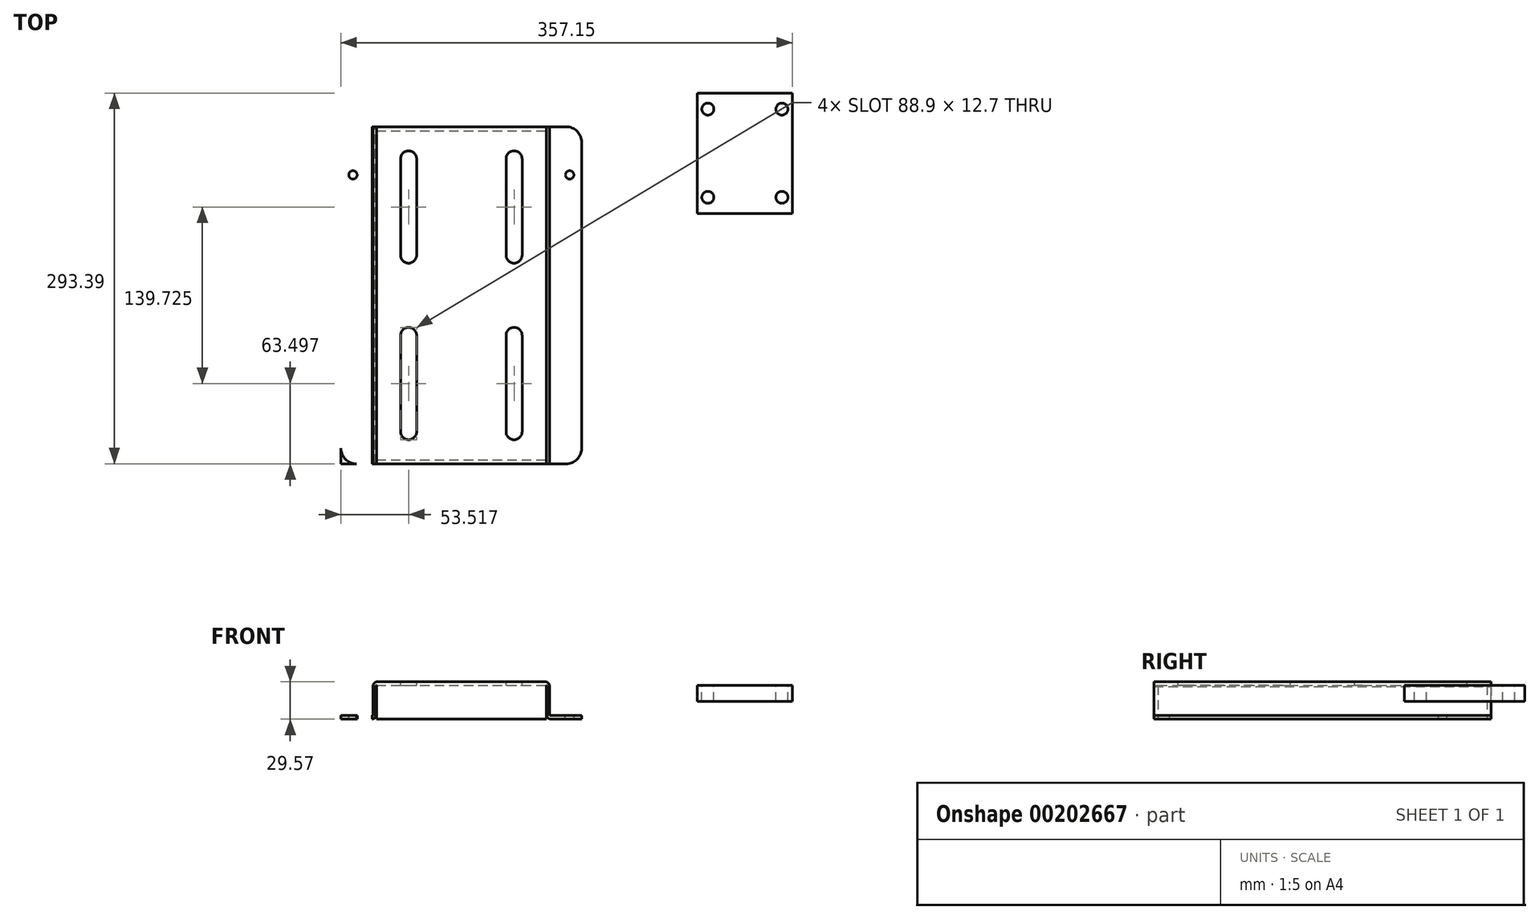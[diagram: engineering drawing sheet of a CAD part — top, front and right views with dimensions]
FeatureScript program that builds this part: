
annotation { "Feature Type Name" : "Feature", "Feature Type Description" : "" }
export const myFeature = defineFeature(function(context is Context, id is Id, definition is map)
    precondition{}
    {
        {
            var Q0;
            Q0=qCreatedBy(makeId("Front.planeOp"),FACE);
            var sketch = newSketch(context, id + "F0", { "sketchPlane" : qUnion([Q0])});
            skLineSegment(sketch, "E0", {"start": v(497.25, 316.92) * mm, "end": v(496.14, 315.8) * mm});
            skLineSegment(sketch, "E1", {"start": v(496.14, 298.54) * mm, "end": v(497.25, 297.42) * mm});
            skLineSegment(sketch, "E2", {"start": v(506.12, 296.17) * mm, "end": v(508.12, 296.17) * mm});
            skLineSegment(sketch, "E3", {"start": v(508.12, 318.17) * mm, "end": v(506.12, 318.17) * mm});
            skLineSegment(sketch, "E4", {"start": v(514.93, 297.83) * mm, "end": v(516.85, 299.75) * mm});
            skLineSegment(sketch, "E5", {"start": v(516.85, 314.6) * mm, "end": v(514.86, 316.59) * mm});
            skLineSegment(sketch, "E6", {"start": v(408.26, 311.93) * mm, "end": v(407.26, 310.93) * mm});
            skLineSegment(sketch, "E7", {"start": v(407.26, 303.4) * mm, "end": v(408.26, 302.41) * mm});
            skLineSegment(sketch, "E8", {"start": v(508.85, 311.93) * mm, "end": v(508.12, 311.93) * mm});
            skLineSegment(sketch, "E9", {"start": v(496.14, 311.93) * mm, "end": v(430.37, 311.93) * mm});
            skLineSegment(sketch, "E10", {"start": v(411.15, 311.93) * mm, "end": v(408.26, 311.93) * mm});
            skLineSegment(sketch, "E11", {"start": v(408.26, 302.41) * mm, "end": v(411.31, 302.41) * mm});
            skLineSegment(sketch, "E12", {"start": v(430.18, 302.41) * mm, "end": v(496.14, 302.41) * mm});
            skLineSegment(sketch, "E13", {"start": v(508.12, 302.41) * mm, "end": v(508.85, 302.41) * mm});
            skLineSegment(sketch, "E14", {"start": v(413.53, 317.08) * mm, "end": v(413.53, 297.08) * mm});
            skLineSegment(sketch, "E15", {"start": v(415.57, 317.08) * mm, "end": v(413.53, 317.08) * mm});
            skLineSegment(sketch, "E16", {"start": v(415.57, 317.08) * mm, "end": v(415.57, 297.08) * mm});
            skLineSegment(sketch, "E17", {"start": v(415.57, 297.08) * mm, "end": v(413.53, 297.08) * mm});
            skLineSegment(sketch, "E18", {"start": v(424.65, 317.08) * mm, "end": v(415.57, 317.08) * mm});
            skLineSegment(sketch, "E19", {"start": v(424.65, 317.08) * mm, "end": v(424.65, 297.08) * mm});
            skLineSegment(sketch, "E20", {"start": v(424.65, 297.08) * mm, "end": v(415.57, 297.08) * mm});
            skLineSegment(sketch, "E21", {"start": v(426.63, 317.08) * mm, "end": v(424.65, 317.08) * mm});
            skLineSegment(sketch, "E22", {"start": v(426.63, 317.08) * mm, "end": v(426.63, 297.08) * mm});
            skLineSegment(sketch, "E23", {"start": v(426.63, 297.08) * mm, "end": v(424.65, 297.08) * mm});
            skLineSegment(sketch, "E24", {"start": v(431.3, 312.33) * mm, "end": v(430.67, 312.15) * mm});
            skLineSegment(sketch, "E25", {"start": v(430.67, 312.15) * mm, "end": v(430.07, 311.63) * mm});
            skLineSegment(sketch, "E26", {"start": v(430.07, 311.63) * mm, "end": v(429.56, 310.8) * mm});
            skLineSegment(sketch, "E27", {"start": v(429.56, 310.8) * mm, "end": v(429.17, 309.7) * mm});
            skLineSegment(sketch, "E28", {"start": v(429.17, 309.7) * mm, "end": v(428.92, 308.44) * mm});
            skLineSegment(sketch, "E29", {"start": v(428.92, 308.44) * mm, "end": v(428.84, 307.08) * mm});
            skLineSegment(sketch, "E30", {"start": v(428.84, 307.08) * mm, "end": v(428.92, 305.72) * mm});
            skLineSegment(sketch, "E31", {"start": v(428.92, 305.72) * mm, "end": v(429.17, 304.46) * mm});
            skLineSegment(sketch, "E32", {"start": v(429.17, 304.46) * mm, "end": v(429.56, 303.37) * mm});
            skLineSegment(sketch, "E33", {"start": v(429.56, 303.37) * mm, "end": v(430.07, 302.53) * mm});
            skLineSegment(sketch, "E34", {"start": v(430.07, 302.53) * mm, "end": v(430.67, 302) * mm});
            skLineSegment(sketch, "E35", {"start": v(430.67, 302) * mm, "end": v(431.3, 301.83) * mm});
            skLineSegment(sketch, "E36", {"start": v(431.3, 301.83) * mm, "end": v(435.98, 301.83) * mm});
            skLineSegment(sketch, "E37", {"start": v(435.98, 301.83) * mm, "end": v(435.98, 297.08) * mm});
            skLineSegment(sketch, "E38", {"start": v(435.98, 317.08) * mm, "end": v(435.98, 312.33) * mm});
            skLineSegment(sketch, "E39", {"start": v(435.98, 312.33) * mm, "end": v(431.3, 312.33) * mm});
            skLineSegment(sketch, "E40", {"start": v(435.98, 317.08) * mm, "end": v(426.63, 317.08) * mm});
            skLineSegment(sketch, "E41", {"start": v(435.98, 297.08) * mm, "end": v(426.63, 297.08) * mm});
            skLineSegment(sketch, "E42", {"start": v(410.31, 301.83) * mm, "end": v(410.88, 302) * mm});
            skLineSegment(sketch, "E43", {"start": v(410.88, 302) * mm, "end": v(411.4, 302.53) * mm});
            skLineSegment(sketch, "E44", {"start": v(411.4, 302.53) * mm, "end": v(411.86, 303.37) * mm});
            skLineSegment(sketch, "E45", {"start": v(411.86, 303.37) * mm, "end": v(412.2, 304.46) * mm});
            skLineSegment(sketch, "E46", {"start": v(412.2, 304.46) * mm, "end": v(412.43, 305.72) * mm});
            skLineSegment(sketch, "E47", {"start": v(412.43, 305.72) * mm, "end": v(412.5, 307.08) * mm});
            skLineSegment(sketch, "E48", {"start": v(412.5, 307.08) * mm, "end": v(412.43, 308.44) * mm});
            skLineSegment(sketch, "E49", {"start": v(412.43, 308.44) * mm, "end": v(412.2, 309.7) * mm});
            skLineSegment(sketch, "E50", {"start": v(412.2, 309.7) * mm, "end": v(411.86, 310.8) * mm});
            skLineSegment(sketch, "E51", {"start": v(411.86, 310.8) * mm, "end": v(411.4, 311.63) * mm});
            skLineSegment(sketch, "E52", {"start": v(411.4, 311.63) * mm, "end": v(410.88, 312.15) * mm});
            skLineSegment(sketch, "E53", {"start": v(410.88, 312.15) * mm, "end": v(410.31, 312.33) * mm});
            skLineSegment(sketch, "E54", {"start": v(410.31, 312.33) * mm, "end": v(405.47, 312.33) * mm});
            skLineSegment(sketch, "E55", {"start": v(405.47, 317.08) * mm, "end": v(405.47, 312.33) * mm});
            skLineSegment(sketch, "E56", {"start": v(413.53, 317.08) * mm, "end": v(405.47, 317.08) * mm});
            skLineSegment(sketch, "E57", {"start": v(405.47, 301.83) * mm, "end": v(405.47, 297.08) * mm});
            skLineSegment(sketch, "E58", {"start": v(405.47, 301.83) * mm, "end": v(410.31, 301.83) * mm});
            skLineSegment(sketch, "E59", {"start": v(413.53, 297.08) * mm, "end": v(405.47, 297.08) * mm});
            skLineSegment(sketch, "E60", {"start": v(496.14, 298.54) * mm, "end": v(496.14, 315.8) * mm});
            skArc(sketch, "E61", {"start": v(497.9, 317.47) * mm, "mid": v(496.52, 314.28) * mm, "end": v(497.9, 311.09) * mm});
            skArc(sketch, "E62", {"start": v(497.9, 311.09) * mm, "mid": v(496.51, 305.94) * mm, "end": v(497.9, 300.8) * mm});
            skLineSegment(sketch, "E63", {"start": v(497.9, 300.8) * mm, "end": v(497, 299.98) * mm});
            skLineSegment(sketch, "E64", {"start": v(497, 299.98) * mm, "end": v(496.53, 299.08) * mm});
            skLineSegment(sketch, "E65", {"start": v(496.53, 299.08) * mm, "end": v(496.56, 298.45) * mm});
            skLineSegment(sketch, "E66", {"start": v(496.56, 298.45) * mm, "end": v(496.9, 297.82) * mm});
            skLineSegment(sketch, "E67", {"start": v(496.9, 297.82) * mm, "end": v(497.9, 296.88) * mm});
            skLineSegment(sketch, "E68", {"start": v(497.28, 316.89) * mm, "end": v(497.9, 317.47) * mm});
            skLineSegment(sketch, "E69", {"start": v(504.14, 300.8) * mm, "end": v(497.9, 300.8) * mm});
            skLineSegment(sketch, "E70", {"start": v(504.14, 311.09) * mm, "end": v(497.9, 311.09) * mm});
            skLineSegment(sketch, "E71", {"start": v(504.14, 317.47) * mm, "end": v(497.9, 317.47) * mm});
            skLineSegment(sketch, "E72", {"start": v(504.14, 296.88) * mm, "end": v(497.9, 296.88) * mm});
            skLineSegment(sketch, "E73", {"start": v(508.12, 318.17) * mm, "end": v(508.12, 296.17) * mm});
            skLineSegment(sketch, "E74", {"start": v(516.85, 299.75) * mm, "end": v(516.85, 314.6) * mm});
            skLineSegment(sketch, "E75", {"start": v(514.85, 297.75) * mm, "end": v(514.92, 297.83) * mm});
            skArc(sketch, "E76", {"start": v(514.85, 297.75) * mm, "mid": v(516.1, 300.17) * mm, "end": v(514.85, 302.6) * mm});
            skArc(sketch, "E77", {"start": v(514.85, 302.6) * mm, "mid": v(516.11, 307.3) * mm, "end": v(514.85, 312.01) * mm});
            skArc(sketch, "E78", {"start": v(514.85, 312.01) * mm, "mid": v(516.1, 314.3) * mm, "end": v(514.85, 316.6) * mm});
            skLineSegment(sketch, "E79", {"start": v(514.85, 302.6) * mm, "end": v(508.85, 302.6) * mm});
            skLineSegment(sketch, "E80", {"start": v(508.85, 302.6) * mm, "end": v(508.85, 312.01) * mm});
            skLineSegment(sketch, "E81", {"start": v(514.85, 312.01) * mm, "end": v(508.85, 312.01) * mm});
            skLineSegment(sketch, "E82", {"start": v(514.85, 297.75) * mm, "end": v(508.85, 297.75) * mm});
            skLineSegment(sketch, "E83", {"start": v(508.85, 297.75) * mm, "end": v(508.85, 302.6) * mm});
            skLineSegment(sketch, "E84", {"start": v(514.85, 316.6) * mm, "end": v(508.85, 316.6) * mm});
            skLineSegment(sketch, "E85", {"start": v(508.85, 312.01) * mm, "end": v(508.85, 316.6) * mm});
            skLineSegment(sketch, "E86", {"start": v(407.26, 307.87) * mm, "end": v(407.26, 310.93) * mm});
            skLineSegment(sketch, "E87", {"start": v(407.26, 303.4) * mm, "end": v(407.26, 307.87) * mm});
            skLineSegment(sketch, "E88", {"start": v(408.26, 308.06) * mm, "end": v(408.26, 302.41) * mm});
            skLineSegment(sketch, "E89", {"start": v(408.26, 311.93) * mm, "end": v(408.26, 308.06) * mm});
            skLineSegment(sketch, "E90", {"start": v(314.3, 351) * mm, "end": v(307.93, 353.74) * mm});
            skLineSegment(sketch, "E91", {"start": v(307.93, 353.74) * mm, "end": v(307.12, 360.62) * mm});
            skLineSegment(sketch, "E92", {"start": v(307.12, 360.62) * mm, "end": v(312.67, 364.76) * mm});
            skLineSegment(sketch, "E93", {"start": v(312.67, 364.76) * mm, "end": v(319.03, 362.02) * mm});
            skLineSegment(sketch, "E94", {"start": v(319.03, 362.02) * mm, "end": v(319.84, 355.14) * mm});
            skLineSegment(sketch, "E95", {"start": v(319.84, 355.14) * mm, "end": v(314.3, 351) * mm});
            skCircle(sketch, "E96", {"center": v(313.48, 357.88) * mm, "radius": 5 * mm});
            skLineSegment(sketch, "E97", {"start": v(435, 351) * mm, "end": v(428.63, 353.73) * mm});
            skLineSegment(sketch, "E98", {"start": v(428.63, 353.73) * mm, "end": v(427.8, 360.6) * mm});
            skLineSegment(sketch, "E99", {"start": v(427.8, 360.6) * mm, "end": v(433.35, 364.76) * mm});
            skLineSegment(sketch, "E100", {"start": v(433.35, 364.76) * mm, "end": v(439.72, 362.03) * mm});
            skLineSegment(sketch, "E101", {"start": v(439.72, 362.03) * mm, "end": v(440.54, 355.16) * mm});
            skLineSegment(sketch, "E102", {"start": v(440.54, 355.16) * mm, "end": v(435, 351) * mm});
            skCircle(sketch, "E103", {"center": v(434.17, 357.88) * mm, "radius": 5 * mm});
            skLineSegment(sketch, "E104", {"start": v(435, 249.54) * mm, "end": v(428.63, 252.27) * mm});
            skLineSegment(sketch, "E105", {"start": v(428.63, 252.27) * mm, "end": v(427.8, 259.14) * mm});
            skLineSegment(sketch, "E106", {"start": v(427.8, 259.14) * mm, "end": v(433.35, 263.3) * mm});
            skLineSegment(sketch, "E107", {"start": v(433.35, 263.3) * mm, "end": v(439.72, 260.57) * mm});
            skLineSegment(sketch, "E108", {"start": v(439.72, 260.57) * mm, "end": v(440.54, 253.7) * mm});
            skLineSegment(sketch, "E109", {"start": v(440.54, 253.7) * mm, "end": v(435, 249.54) * mm});
            skCircle(sketch, "E110", {"center": v(434.17, 256.42) * mm, "radius": 5 * mm});
            skLineSegment(sketch, "E111", {"start": v(314.3, 249.54) * mm, "end": v(307.94, 252.27) * mm});
            skLineSegment(sketch, "E112", {"start": v(307.94, 252.27) * mm, "end": v(307.11, 259.14) * mm});
            skLineSegment(sketch, "E113", {"start": v(307.11, 259.14) * mm, "end": v(312.66, 263.3) * mm});
            skLineSegment(sketch, "E114", {"start": v(312.66, 263.3) * mm, "end": v(319.03, 260.57) * mm});
            skLineSegment(sketch, "E115", {"start": v(319.03, 260.57) * mm, "end": v(319.85, 253.7) * mm});
            skLineSegment(sketch, "E116", {"start": v(319.85, 253.7) * mm, "end": v(314.3, 249.54) * mm});
            skCircle(sketch, "E117", {"center": v(313.48, 256.42) * mm, "radius": 5 * mm});
            skLineSegment(sketch, "E118", {"start": v(456.35, 372.53) * mm, "end": v(291.48, 372.53) * mm});
            skLineSegment(sketch, "E119", {"start": v(456.35, 370.43) * mm, "end": v(456.35, 372.53) * mm});
            skLineSegment(sketch, "E120", {"start": v(456.35, 370.43) * mm, "end": v(291.48, 370.43) * mm});
            skLineSegment(sketch, "E121", {"start": v(291.48, 370.43) * mm, "end": v(291.48, 372.53) * mm});
            skLineSegment(sketch, "E122", {"start": v(456.35, 242.13) * mm, "end": v(456.35, 244.1) * mm});
            skLineSegment(sketch, "E123", {"start": v(456.35, 242.13) * mm, "end": v(291.48, 242.13) * mm});
            skLineSegment(sketch, "E124", {"start": v(456.35, 244.1) * mm, "end": v(291.48, 244.1) * mm});
            skLineSegment(sketch, "E125", {"start": v(291.48, 242.13) * mm, "end": v(291.48, 244.1) * mm});
            skLineSegment(sketch, "E126", {"start": v(456.35, 244.84) * mm, "end": v(291.48, 244.84) * mm});
            skLineSegment(sketch, "E127", {"start": v(456.35, 244.1) * mm, "end": v(456.35, 244.84) * mm});
            skLineSegment(sketch, "E128", {"start": v(291.48, 244.1) * mm, "end": v(291.48, 244.84) * mm});
            skLineSegment(sketch, "E129", {"start": v(456.35, 369.7) * mm, "end": v(456.35, 370.43) * mm});
            skLineSegment(sketch, "E130", {"start": v(456.35, 369.7) * mm, "end": v(291.48, 369.7) * mm});
            skLineSegment(sketch, "E131", {"start": v(291.48, 369.7) * mm, "end": v(291.48, 370.43) * mm});
            skLineSegment(sketch, "E132", {"start": v(456.35, 244.84) * mm, "end": v(456.35, 302.41) * mm});
            skLineSegment(sketch, "E133", {"start": v(456.35, 311.93) * mm, "end": v(456.35, 369.7) * mm});
            skLineSegment(sketch, "E134", {"start": v(291.48, 244.84) * mm, "end": v(291.48, 369.7) * mm});
            skArc(sketch, "E135", {"start": v(239.39, 226.88) * mm, "mid": v(243.78, 216.27) * mm, "end": v(254.39, 211.88) * mm});
            skLineSegment(sketch, "E136", {"start": v(239.39, 226.88) * mm, "end": v(239.39, 236.54) * mm});
            skLineSegment(sketch, "E137", {"start": v(506.12, 236.54) * mm, "end": v(239.39, 236.54) * mm});
            skLineSegment(sketch, "E138", {"start": v(506.12, 226.88) * mm, "end": v(506.12, 236.54) * mm});
            skArc(sketch, "E139", {"start": v(491.12, 211.88) * mm, "mid": v(501.72, 216.27) * mm, "end": v(506.12, 226.88) * mm});
            skLineSegment(sketch, "E140", {"start": v(491.12, 211.88) * mm, "end": v(254.39, 211.88) * mm});
            skCircle(sketch, "E141", {"center": v(279.12, 221.4) * mm, "radius": 4.76 * mm});
            skCircle(sketch, "E142", {"center": v(469.48, 221.4) * mm, "radius": 4.76 * mm});
            skLineSegment(sketch, "E143", {"start": v(506.12, 239.26) * mm, "end": v(239.39, 239.26) * mm});
            skLineSegment(sketch, "E144", {"start": v(506.12, 236.54) * mm, "end": v(506.12, 239.26) * mm});
            skLineSegment(sketch, "E145", {"start": v(239.39, 236.54) * mm, "end": v(239.39, 239.26) * mm});
            skLineSegment(sketch, "E146", {"start": v(239.39, 240) * mm, "end": v(241.37, 240) * mm});
            skLineSegment(sketch, "E147", {"start": v(239.39, 374.27) * mm, "end": v(239.39, 240) * mm});
            skLineSegment(sketch, "E148", {"start": v(239.39, 374.27) * mm, "end": v(241.37, 374.27) * mm});
            skLineSegment(sketch, "E149", {"start": v(241.37, 374.27) * mm, "end": v(241.37, 240) * mm});
            skArc(sketch, "E150", {"start": v(506.12, 387.38) * mm, "mid": v(501.72, 397.99) * mm, "end": v(491.12, 402.38) * mm});
            skLineSegment(sketch, "E151", {"start": v(506.12, 377.72) * mm, "end": v(506.12, 387.38) * mm});
            skLineSegment(sketch, "E152", {"start": v(506.12, 377.72) * mm, "end": v(239.39, 377.72) * mm});
            skLineSegment(sketch, "E153", {"start": v(491.12, 402.38) * mm, "end": v(254.39, 402.38) * mm});
            skCircle(sketch, "E154", {"center": v(279.12, 392.86) * mm, "radius": 4.76 * mm});
            skCircle(sketch, "E155", {"center": v(469.48, 392.86) * mm, "radius": 4.76 * mm});
            skLineSegment(sketch, "E156", {"start": v(239.39, 377.72) * mm, "end": v(239.39, 387.38) * mm});
            skArc(sketch, "E157", {"start": v(254.39, 402.38) * mm, "mid": v(243.78, 397.99) * mm, "end": v(239.39, 387.38) * mm});
            skLineSegment(sketch, "E158", {"start": v(506.12, 375) * mm, "end": v(506.12, 377.72) * mm});
            skLineSegment(sketch, "E159", {"start": v(506.12, 375) * mm, "end": v(239.39, 375) * mm});
            skLineSegment(sketch, "E160", {"start": v(239.39, 375) * mm, "end": v(239.39, 377.72) * mm});
            skLineSegment(sketch, "E161", {"start": v(506.12, 374.27) * mm, "end": v(504.14, 374.27) * mm});
            skLineSegment(sketch, "E162", {"start": v(506.12, 240) * mm, "end": v(506.12, 374.27) * mm});
            skLineSegment(sketch, "E163", {"start": v(506.12, 240) * mm, "end": v(504.14, 240) * mm});
            skLineSegment(sketch, "E164", {"start": v(504.14, 240) * mm, "end": v(504.14, 374.27) * mm});
            skLineSegment(sketch, "E165", {"start": v(503.4, 240) * mm, "end": v(242.1, 240) * mm});
            skLineSegment(sketch, "E166", {"start": v(506.12, 239.26) * mm, "end": v(506.12, 240) * mm});
            skLineSegment(sketch, "E167", {"start": v(239.39, 239.26) * mm, "end": v(239.39, 240) * mm});
            skLineSegment(sketch, "E168", {"start": v(506.12, 374.27) * mm, "end": v(506.12, 375) * mm});
            skLineSegment(sketch, "E169", {"start": v(503.4, 374.27) * mm, "end": v(242.1, 374.27) * mm});
            skLineSegment(sketch, "E170", {"start": v(239.39, 374.27) * mm, "end": v(239.39, 375) * mm});
            skLineSegment(sketch, "E171", {"start": v(242.1, 240) * mm, "end": v(242.1, 374.27) * mm});
            skLineSegment(sketch, "E172", {"start": v(242.1, 374.27) * mm, "end": v(241.37, 374.27) * mm});
            skLineSegment(sketch, "E173", {"start": v(241.37, 240) * mm, "end": v(242.1, 240) * mm});
            skLineSegment(sketch, "E174", {"start": v(503.4, 240) * mm, "end": v(504.14, 240) * mm});
            skLineSegment(sketch, "E175", {"start": v(504.14, 374.27) * mm, "end": v(503.4, 374.27) * mm});
            skLineSegment(sketch, "E176", {"start": v(456.35, 251.47) * mm, "end": v(471.2, 251.47) * mm});
            skArc(sketch, "E177", {"start": v(471.2, 251.47) * mm, "mid": v(475.94, 256.22) * mm, "end": v(471.2, 260.97) * mm});
            skLineSegment(sketch, "E178", {"start": v(471.2, 260.97) * mm, "end": v(456.35, 260.97) * mm});
            skLineSegment(sketch, "E179", {"start": v(291.48, 362.43) * mm, "end": v(275.26, 362.43) * mm});
            skArc(sketch, "E180", {"start": v(275.26, 362.43) * mm, "mid": v(270.51, 357.68) * mm, "end": v(275.26, 352.93) * mm});
            skLineSegment(sketch, "E181", {"start": v(275.26, 352.93) * mm, "end": v(291.48, 352.93) * mm});
            skLineSegment(sketch, "E182", {"start": v(291.48, 260.97) * mm, "end": v(275.94, 260.97) * mm});
            skArc(sketch, "E183", {"start": v(275.94, 260.97) * mm, "mid": v(271.2, 256.22) * mm, "end": v(275.94, 251.47) * mm});
            skLineSegment(sketch, "E184", {"start": v(291.48, 251.47) * mm, "end": v(275.94, 251.47) * mm});
            skArc(sketch, "E185", {"start": v(471.2, 352.93) * mm, "mid": v(475.94, 357.68) * mm, "end": v(471.2, 362.43) * mm});
            skLineSegment(sketch, "E186", {"start": v(471.2, 362.43) * mm, "end": v(456.35, 362.43) * mm});
            skLineSegment(sketch, "E187", {"start": v(471.2, 352.93) * mm, "end": v(456.35, 352.93) * mm});
            skLineSegment(sketch, "E188", {"start": v(503.4, 374.27) * mm, "end": v(503.4, 317.47) * mm});
            skLineSegment(sketch, "E189", {"start": v(503.4, 296.88) * mm, "end": v(503.4, 240) * mm});
            skLineSegment(sketch, "E190", {"start": v(279.12, 400) * mm, "end": v(279.12, 385.71) * mm});
            skLineSegment(sketch, "E191", {"start": v(269.36, 392.86) * mm, "end": v(285.6, 392.86) * mm});
            skLineSegment(sketch, "E192", {"start": v(279.12, 228.55) * mm, "end": v(279.12, 214.26) * mm});
            skLineSegment(sketch, "E193", {"start": v(269.14, 221.4) * mm, "end": v(285.82, 221.4) * mm});
            skLineSegment(sketch, "E194", {"start": v(461.08, 221.4) * mm, "end": v(477.89, 221.4) * mm});
            skLineSegment(sketch, "E195", {"start": v(469.48, 228.55) * mm, "end": v(469.48, 214.26) * mm});
            skLineSegment(sketch, "E196", {"start": v(469.48, 400) * mm, "end": v(469.48, 385.71) * mm});
            skLineSegment(sketch, "E197", {"start": v(462.06, 392.86) * mm, "end": v(476.9, 392.86) * mm});
            skLineSegment(sketch, "E198", {"start": v(296.76, 388.38) * mm, "end": v(295.07, 390.07) * mm});
            skLineSegment(sketch, "E199", {"start": v(282.91, 390.07) * mm, "end": v(281.22, 388.38) * mm});
            skLineSegment(sketch, "E200", {"start": v(398.23, 388.38) * mm, "end": v(396.54, 390.07) * mm});
            skLineSegment(sketch, "E201", {"start": v(384.38, 390.07) * mm, "end": v(382.69, 388.38) * mm});
            skLineSegment(sketch, "E202", {"start": v(381.46, 382.07) * mm, "end": v(381.46, 380.57) * mm});
            skLineSegment(sketch, "E203", {"start": v(399.46, 380.57) * mm, "end": v(399.46, 382.07) * mm});
            skLineSegment(sketch, "E204", {"start": v(279.86, 382.07) * mm, "end": v(279.86, 380.57) * mm});
            skLineSegment(sketch, "E205", {"start": v(298, 380.57) * mm, "end": v(298, 382.07) * mm});
            skLineSegment(sketch, "E206", {"start": v(293, 390.07) * mm, "end": v(293, 400.16) * mm});
            skLineSegment(sketch, "E207", {"start": v(285, 400.16) * mm, "end": v(285, 390.07) * mm});
            skLineSegment(sketch, "E208", {"start": v(293, 400.16) * mm, "end": v(292, 401.16) * mm});
            skLineSegment(sketch, "E209", {"start": v(286, 401.16) * mm, "end": v(285, 400.16) * mm});
            skLineSegment(sketch, "E210", {"start": v(394.46, 390.07) * mm, "end": v(394.46, 400.16) * mm});
            skLineSegment(sketch, "E211", {"start": v(386.46, 400.16) * mm, "end": v(386.46, 390.07) * mm});
            skLineSegment(sketch, "E212", {"start": v(394.46, 400.16) * mm, "end": v(393.46, 401.16) * mm});
            skLineSegment(sketch, "E213", {"start": v(387.46, 401.16) * mm, "end": v(386.46, 400.16) * mm});
            skCircle(sketch, "E214", {"center": v(339.7, 366.58) * mm, "radius": 11 * mm});
            skCircle(sketch, "E215", {"center": v(339.7, 366.58) * mm, "radius": 7.42 * mm});
            skLineSegment(sketch, "E216", {"start": v(349.12, 366.43) * mm, "end": v(344.54, 374.66) * mm});
            skLineSegment(sketch, "E217", {"start": v(344.28, 358.34) * mm, "end": v(349.12, 366.43) * mm});
            skLineSegment(sketch, "E218", {"start": v(334.86, 358.5) * mm, "end": v(344.28, 358.34) * mm});
            skLineSegment(sketch, "E219", {"start": v(330.28, 366.73) * mm, "end": v(334.86, 358.5) * mm});
            skLineSegment(sketch, "E220", {"start": v(335.12, 374.81) * mm, "end": v(330.28, 366.73) * mm});
            skLineSegment(sketch, "E221", {"start": v(344.54, 374.66) * mm, "end": v(335.12, 374.81) * mm});
            skLineSegment(sketch, "E222", {"start": v(284.4, 382.07) * mm, "end": v(284.4, 388.07) * mm});
            skArc(sketch, "E223", {"start": v(292.46, 388.07) * mm, "mid": v(288.43, 389.15) * mm, "end": v(284.4, 388.07) * mm});
            skLineSegment(sketch, "E224", {"start": v(292.46, 382.07) * mm, "end": v(292.46, 388.07) * mm});
            skLineSegment(sketch, "E225", {"start": v(296.74, 388.36) * mm, "end": v(297.05, 388.07) * mm});
            skArc(sketch, "E226", {"start": v(297.05, 388.07) * mm, "mid": v(294.75, 389.15) * mm, "end": v(292.46, 388.07) * mm});
            skLineSegment(sketch, "E227", {"start": v(284.4, 388.07) * mm, "end": v(283.68, 388.77) * mm});
            skLineSegment(sketch, "E228", {"start": v(283.68, 388.77) * mm, "end": v(282.89, 389.14) * mm});
            skLineSegment(sketch, "E229", {"start": v(282.89, 389.14) * mm, "end": v(281.77, 388.85) * mm});
            skLineSegment(sketch, "E230", {"start": v(281.77, 388.85) * mm, "end": v(280.94, 388.07) * mm});
            skLineSegment(sketch, "E231", {"start": v(282.91, 390.07) * mm, "end": v(295.07, 390.07) * mm});
            skLineSegment(sketch, "E232", {"start": v(297.05, 382.07) * mm, "end": v(297.05, 388.07) * mm});
            skLineSegment(sketch, "E233", {"start": v(280.94, 382.07) * mm, "end": v(280.94, 388.07) * mm});
            skLineSegment(sketch, "E234", {"start": v(398.2, 388.36) * mm, "end": v(398.51, 388.07) * mm});
            skArc(sketch, "E235", {"start": v(398.51, 388.07) * mm, "mid": v(396.22, 389.15) * mm, "end": v(393.92, 388.07) * mm});
            skArc(sketch, "E236", {"start": v(393.92, 388.07) * mm, "mid": v(389.9, 389.15) * mm, "end": v(385.87, 388.07) * mm});
            skLineSegment(sketch, "E237", {"start": v(385.87, 388.07) * mm, "end": v(385.14, 388.77) * mm});
            skLineSegment(sketch, "E238", {"start": v(385.14, 388.77) * mm, "end": v(384.35, 389.14) * mm});
            skLineSegment(sketch, "E239", {"start": v(384.35, 389.14) * mm, "end": v(383.23, 388.85) * mm});
            skLineSegment(sketch, "E240", {"start": v(383.23, 388.85) * mm, "end": v(382.4, 388.07) * mm});
            skLineSegment(sketch, "E241", {"start": v(384.38, 390.07) * mm, "end": v(396.54, 390.07) * mm});
            skLineSegment(sketch, "E242", {"start": v(385.87, 382.07) * mm, "end": v(385.87, 388.07) * mm});
            skLineSegment(sketch, "E243", {"start": v(393.92, 382.07) * mm, "end": v(393.92, 388.07) * mm});
            skLineSegment(sketch, "E244", {"start": v(398.51, 382.07) * mm, "end": v(398.51, 388.07) * mm});
            skLineSegment(sketch, "E245", {"start": v(382.4, 382.07) * mm, "end": v(382.4, 388.07) * mm});
            skLineSegment(sketch, "E246", {"start": v(399.46, 382.07) * mm, "end": v(381.46, 382.07) * mm});
            skLineSegment(sketch, "E247", {"start": v(298, 382.07) * mm, "end": v(279.86, 382.07) * mm});
            skLineSegment(sketch, "E248", {"start": v(293, 400.16) * mm, "end": v(285, 400.16) * mm});
            skLineSegment(sketch, "E249", {"start": v(286, 401.16) * mm, "end": v(292, 401.16) * mm});
            skLineSegment(sketch, "E250", {"start": v(394.46, 400.16) * mm, "end": v(386.46, 400.16) * mm});
            skLineSegment(sketch, "E251", {"start": v(387.46, 401.16) * mm, "end": v(393.46, 401.16) * mm});
            skLineSegment(sketch, "E252", {"start": v(272.6, 351) * mm, "end": v(272.6, 376.86) * mm});
            skLineSegment(sketch, "E253", {"start": v(406.88, 376.86) * mm, "end": v(406.88, 351) * mm});
            skLineSegment(sketch, "E254", {"start": v(406.88, 351) * mm, "end": v(272.6, 351) * mm});
            skLineSegment(sketch, "E255", {"start": v(269.15, 351) * mm, "end": v(269.15, 353.98) * mm});
            skLineSegment(sketch, "E256", {"start": v(269.15, 351) * mm, "end": v(259.5, 351) * mm});
            skLineSegment(sketch, "E257", {"start": v(259.5, 353.98) * mm, "end": v(259.5, 351) * mm});
            skLineSegment(sketch, "E258", {"start": v(269.15, 353.98) * mm, "end": v(259.5, 353.98) * mm});
            skLineSegment(sketch, "E259", {"start": v(271.87, 376.86) * mm, "end": v(269.9, 376.86) * mm});
            skLineSegment(sketch, "E260", {"start": v(271.87, 376.86) * mm, "end": v(271.87, 353.72) * mm});
            skLineSegment(sketch, "E261", {"start": v(269.9, 354.72) * mm, "end": v(271.87, 353.72) * mm});
            skLineSegment(sketch, "E262", {"start": v(269.9, 376.86) * mm, "end": v(269.9, 354.72) * mm});
            skLineSegment(sketch, "E263", {"start": v(410.33, 353.98) * mm, "end": v(410.33, 351) * mm});
            skLineSegment(sketch, "E264", {"start": v(420, 353.98) * mm, "end": v(410.33, 353.98) * mm});
            skLineSegment(sketch, "E265", {"start": v(420, 351) * mm, "end": v(420, 353.98) * mm});
            skLineSegment(sketch, "E266", {"start": v(420, 351) * mm, "end": v(410.33, 351) * mm});
            skArc(sketch, "E267", {"start": v(269.15, 351) * mm, "mid": v(271.08, 351.8) * mm, "end": v(271.87, 353.72) * mm});
            skArc(sketch, "E268", {"start": v(269.15, 353.98) * mm, "mid": v(269.68, 354.2) * mm, "end": v(269.9, 354.72) * mm});
            skLineSegment(sketch, "E269", {"start": v(244.5, 351) * mm, "end": v(244.5, 353.98) * mm});
            skLineSegment(sketch, "E270", {"start": v(259.5, 351) * mm, "end": v(244.5, 351) * mm});
            skLineSegment(sketch, "E271", {"start": v(244.5, 353.98) * mm, "end": v(259.5, 353.98) * mm});
            skLineSegment(sketch, "E272", {"start": v(420, 353.98) * mm, "end": v(435, 353.98) * mm});
            skLineSegment(sketch, "E273", {"start": v(435, 353.98) * mm, "end": v(435, 351) * mm});
            skLineSegment(sketch, "E274", {"start": v(435, 351) * mm, "end": v(420, 351) * mm});
            skLineSegment(sketch, "E275", {"start": v(272.6, 380.57) * mm, "end": v(272.6, 377.6) * mm});
            skArc(sketch, "E276", {"start": v(272.6, 377.6) * mm, "mid": v(272.09, 377.38) * mm, "end": v(271.87, 376.86) * mm});
            skArc(sketch, "E277", {"start": v(272.6, 380.57) * mm, "mid": v(270.6, 379.19) * mm, "end": v(269.9, 376.86) * mm});
            skLineSegment(sketch, "E278", {"start": v(407.62, 353.72) * mm, "end": v(409.6, 354.72) * mm});
            skLineSegment(sketch, "E279", {"start": v(409.6, 376.86) * mm, "end": v(407.62, 376.86) * mm});
            skLineSegment(sketch, "E280", {"start": v(409.6, 354.72) * mm, "end": v(409.6, 376.86) * mm});
            skLineSegment(sketch, "E281", {"start": v(407.62, 353.72) * mm, "end": v(407.62, 376.86) * mm});
            skArc(sketch, "E282", {"start": v(409.6, 354.72) * mm, "mid": v(409.81, 354.2) * mm, "end": v(410.33, 353.98) * mm});
            skArc(sketch, "E283", {"start": v(407.62, 353.72) * mm, "mid": v(408.41, 351.8) * mm, "end": v(410.33, 351) * mm});
            skLineSegment(sketch, "E284", {"start": v(272.6, 380.57) * mm, "end": v(406.88, 380.57) * mm});
            skLineSegment(sketch, "E285", {"start": v(272.6, 376.86) * mm, "end": v(272.6, 377.6) * mm});
            skLineSegment(sketch, "E286", {"start": v(406.88, 377.6) * mm, "end": v(406.88, 376.86) * mm});
            skLineSegment(sketch, "E287", {"start": v(406.88, 377.6) * mm, "end": v(406.88, 380.57) * mm});
            skArc(sketch, "E288", {"start": v(407.62, 376.86) * mm, "mid": v(407.4, 377.38) * mm, "end": v(406.88, 377.6) * mm});
            skArc(sketch, "E289", {"start": v(409.6, 376.86) * mm, "mid": v(408.84, 379.16) * mm, "end": v(406.88, 380.57) * mm});
            skLineSegment(sketch, "E290", {"start": v(406.88, 376.86) * mm, "end": v(343.61, 376.86) * mm});
            skLineSegment(sketch, "E291", {"start": v(335.8, 376.86) * mm, "end": v(272.6, 376.86) * mm});
            skLineSegment(sketch, "E292", {"start": v(339.7, 340.96) * mm, "end": v(339.7, 389.56) * mm});
            skLineSegment(sketch, "E293", {"start": v(289, 413.63) * mm, "end": v(289, 364.67) * mm});
            skLineSegment(sketch, "E294", {"start": v(390.46, 413.93) * mm, "end": v(390.46, 364.37) * mm});
            skLineSegment(sketch, "E295", {"start": v(19.56, -106.93) * mm, "end": v(19.56, -108.43) * mm});
            skLineSegment(sketch, "E296", {"start": v(37.56, -108.43) * mm, "end": v(37.56, -106.93) * mm});
            skLineSegment(sketch, "E297", {"start": v(-82.04, -106.93) * mm, "end": v(-82.04, -108.43) * mm});
            skLineSegment(sketch, "E298", {"start": v(-63.9, -108.43) * mm, "end": v(-63.9, -106.93) * mm});
            skLineSegment(sketch, "E299", {"start": v(-89.3, -138) * mm, "end": v(-89.3, -112.14) * mm});
            skLineSegment(sketch, "E300", {"start": v(44.98, -112.14) * mm, "end": v(44.98, -138) * mm});
            skLineSegment(sketch, "E301", {"start": v(44.98, -138) * mm, "end": v(-89.3, -138) * mm});
            skLineSegment(sketch, "E302", {"start": v(-92.75, -138) * mm, "end": v(-92.75, -135.02) * mm});
            skLineSegment(sketch, "E303", {"start": v(-92.75, -138) * mm, "end": v(-102.4, -138) * mm});
            skLineSegment(sketch, "E304", {"start": v(-102.4, -135.02) * mm, "end": v(-102.4, -138) * mm});
            skLineSegment(sketch, "E305", {"start": v(-92.75, -135.02) * mm, "end": v(-102.4, -135.02) * mm});
            skLineSegment(sketch, "E306", {"start": v(-90.03, -112.14) * mm, "end": v(-92, -112.14) * mm});
            skLineSegment(sketch, "E307", {"start": v(-90.03, -112.14) * mm, "end": v(-90.03, -135.28) * mm});
            skLineSegment(sketch, "E308", {"start": v(-92, -134.29) * mm, "end": v(-90.03, -135.28) * mm});
            skLineSegment(sketch, "E309", {"start": v(-92, -112.14) * mm, "end": v(-92, -134.29) * mm});
            skLineSegment(sketch, "E310", {"start": v(48.43, -135.02) * mm, "end": v(48.43, -138) * mm});
            skLineSegment(sketch, "E311", {"start": v(58.1, -135.02) * mm, "end": v(48.43, -135.02) * mm});
            skLineSegment(sketch, "E312", {"start": v(58.1, -138) * mm, "end": v(58.1, -135.02) * mm});
            skLineSegment(sketch, "E313", {"start": v(58.1, -138) * mm, "end": v(48.43, -138) * mm});
            skArc(sketch, "E314", {"start": v(-92.75, -138) * mm, "mid": v(-90.83, -137.2) * mm, "end": v(-90.03, -135.28) * mm});
            skArc(sketch, "E315", {"start": v(-92.75, -135.02) * mm, "mid": v(-92.23, -134.8) * mm, "end": v(-92, -134.29) * mm});
            skLineSegment(sketch, "E316", {"start": v(-117.4, -138) * mm, "end": v(-117.4, -135.02) * mm});
            skLineSegment(sketch, "E317", {"start": v(-102.4, -138) * mm, "end": v(-117.4, -138) * mm});
            skLineSegment(sketch, "E318", {"start": v(-117.4, -135.02) * mm, "end": v(-102.4, -135.02) * mm});
            skLineSegment(sketch, "E319", {"start": v(58.1, -135.02) * mm, "end": v(73.1, -135.02) * mm});
            skLineSegment(sketch, "E320", {"start": v(73.1, -135.02) * mm, "end": v(73.1, -138) * mm});
            skLineSegment(sketch, "E321", {"start": v(73.1, -138) * mm, "end": v(58.1, -138) * mm});
            skLineSegment(sketch, "E322", {"start": v(-89.3, -108.43) * mm, "end": v(-89.3, -111.4) * mm});
            skArc(sketch, "E323", {"start": v(-89.3, -111.4) * mm, "mid": v(-89.81, -111.62) * mm, "end": v(-90.03, -112.14) * mm});
            skArc(sketch, "E324", {"start": v(-89.3, -108.43) * mm, "mid": v(-91.3, -109.82) * mm, "end": v(-92, -112.14) * mm});
            skLineSegment(sketch, "E325", {"start": v(45.72, -135.28) * mm, "end": v(47.7, -134.29) * mm});
            skLineSegment(sketch, "E326", {"start": v(47.7, -112.14) * mm, "end": v(45.72, -112.14) * mm});
            skLineSegment(sketch, "E327", {"start": v(47.7, -134.29) * mm, "end": v(47.7, -112.14) * mm});
            skLineSegment(sketch, "E328", {"start": v(45.72, -135.28) * mm, "end": v(45.72, -112.14) * mm});
            skArc(sketch, "E329", {"start": v(47.7, -134.29) * mm, "mid": v(47.91, -134.8) * mm, "end": v(48.43, -135.02) * mm});
            skArc(sketch, "E330", {"start": v(45.72, -135.28) * mm, "mid": v(46.51, -137.2) * mm, "end": v(48.43, -138) * mm});
            skLineSegment(sketch, "E331", {"start": v(-89.3, -108.43) * mm, "end": v(44.98, -108.43) * mm});
            skLineSegment(sketch, "E332", {"start": v(-89.3, -112.14) * mm, "end": v(-89.3, -111.4) * mm});
            skLineSegment(sketch, "E333", {"start": v(44.98, -111.4) * mm, "end": v(44.98, -112.14) * mm});
            skLineSegment(sketch, "E334", {"start": v(44.98, -111.4) * mm, "end": v(44.98, -108.43) * mm});
            skArc(sketch, "E335", {"start": v(45.72, -112.14) * mm, "mid": v(45.5, -111.62) * mm, "end": v(44.98, -111.4) * mm});
            skArc(sketch, "E336", {"start": v(47.7, -112.14) * mm, "mid": v(46.94, -109.85) * mm, "end": v(44.98, -108.43) * mm});
            skLineSegment(sketch, "E337", {"start": v(44.98, -112.14) * mm, "end": v(-18.3, -112.14) * mm});
            skLineSegment(sketch, "E338", {"start": v(-26.1, -112.14) * mm, "end": v(-89.3, -112.14) * mm});
            skLineSegment(sketch, "E339", {"start": v(-26.1, -112.14) * mm, "end": v(-18.3, -112.14) * mm});
            skLineSegment(sketch, "E340", {"start": v(313.48, 357.88) * mm, "end": v(434.17, 357.88) * mm});
            skLineSegment(sketch, "E341", {"start": v(313.48, 256.42) * mm, "end": v(313.48, 357.88) * mm});
            skLineSegment(sketch, "E342", {"start": v(313.48, 307.15) * mm, "end": v(291.48, 307.15) * mm});
            skLineSegment(sketch, "E343", {"start": v(302.48, 307.15) * mm, "end": v(302.48, 242.13) * mm});
            skLineSegment(sketch, "E344", {"start": v(291.48, 280.64) * mm, "end": v(456.35, 280.64) * mm});
            skSolve(sketch);
        }
        {
            var Q0;
            Q0=makeQuery(id+"F0.imprint","IMPRINT",FACE,{"disambiguationData":[TD([[makeQuery(id+"F0.imprint","IMPRINT",EDGE,{"derivedFrom":sQuery(id+"F0.wireOp",EDGE,"E299")}),-1.0]])]});
            var Q1;
            Q1=makeQuery(id+"F0.imprint","IMPRINT",FACE,{"disambiguationData":[TD([[makeQuery(id+"F0.imprint","IMPRINT",EDGE,{"derivedFrom":sQuery(id+"F0.wireOp",EDGE,"E306")}),1.0]])]});
            var Q2;
            Q2=makeQuery(id+"F0.imprint","IMPRINT",FACE,{"disambiguationData":[TD([[makeQuery(id+"F0.imprint","IMPRINT",EDGE,{"derivedFrom":sQuery(id+"F0.wireOp",EDGE,"E304")}),-1.0]])]});
            var Q3;
            Q3=makeQuery(id+"F0.imprint","IMPRINT",FACE,{"disambiguationData":[TD([[makeQuery(id+"F0.imprint","IMPRINT",EDGE,{"derivedFrom":sQuery(id+"F0.wireOp",EDGE,"E302")}),1.0]])]});
            var Q4;
            Q4=makeQuery(id+"F0.imprint","IMPRINT",FACE,{"disambiguationData":[TD([[makeQuery(id+"F0.imprint","IMPRINT",EDGE,{"derivedFrom":sQuery(id+"F0.wireOp",EDGE,"E302")}),-1.0]])]});
            var Q5;
            Q5=makeQuery(id+"F0.imprint","IMPRINT",FACE,{"disambiguationData":[TD([[makeQuery(id+"F0.imprint","IMPRINT",EDGE,{"derivedFrom":sQuery(id+"F0.wireOp",EDGE,"E306")}),-1.0]])]});
            var Q6;
            {var subQ6=sQuery(id+"F0.wireOp",EDGE,"E322");Q6=makeQuery(id+"F0.imprint","IMPRINT",FACE,{"disambiguationData":[TD([[makeQuery(id+"F0.imprint","IMPRINT",EDGE,{"derivedFrom":subQ6}),1.0]])]});}
            var Q7;
            Q7=makeQuery(id+"F0.imprint","IMPRINT",FACE,{"disambiguationData":[TD([[makeQuery(id+"F0.imprint","IMPRINT",EDGE,{"derivedFrom":sQuery(id+"F0.wireOp",EDGE,"E325")}),1.0]])]});
            var Q8;
            Q8=makeQuery(id+"F0.imprint","IMPRINT",FACE,{"disambiguationData":[TD([[makeQuery(id+"F0.imprint","IMPRINT",EDGE,{"derivedFrom":sQuery(id+"F0.wireOp",EDGE,"E326")}),-1.0]])]});
            var Q9;
            Q9=makeQuery(id+"F0.imprint","IMPRINT",FACE,{"disambiguationData":[TD([[makeQuery(id+"F0.imprint","IMPRINT",EDGE,{"derivedFrom":sQuery(id+"F0.wireOp",EDGE,"E310")}),1.0]])]});
            var Q10;
            Q10=makeQuery(id+"F0.imprint","IMPRINT",FACE,{"disambiguationData":[TD([[makeQuery(id+"F0.imprint","IMPRINT",EDGE,{"derivedFrom":sQuery(id+"F0.wireOp",EDGE,"E312")}),-1.0]])]});
            var Q11;
            Q11=makeQuery(id+"F0.imprint","IMPRINT",FACE,{"disambiguationData":[TD([[makeQuery(id+"F0.imprint","IMPRINT",EDGE,{"derivedFrom":sQuery(id+"F0.wireOp",EDGE,"E310")}),-1.0]])]});
            extrude(context, id + "F1", {"entities" : qUnion([Q0, Q1, Q2, Q3, Q4, Q5, Q6, Q7, Q8, Q9, Q10, Q11]), "endBound" : BoundingType.SYMMETRIC, "depth" : 266.73 * mm});
        }
        {
            var Q0;
            Q0=makeQuery(id+"F1.opExtrude","SWEPT_FACE",FACE,{"disambiguationData":[OSD([sQuery(id+"F0.wireOp",EDGE,"E331")])]});
            var sketch = newSketch(context, id + "F2", { "sketchPlane" : qUnion([Q0])});
            skSolve(sketch);
        }
        {
            var Q0;
            {var subQ0=sQuery(id+"F0.wireOp",EDGE,"E331");Q0=makeQuery(id+"F2.imprint","IMPRINT",FACE,{"disambiguationData":[TD([[makeQuery(id+"F2.imprint","IMPRINT",EDGE,{"derivedFrom":makeQuery(id+"F1.opExtrude","CAP_EDGE",EDGE,{"disambiguationData":[OSD([subQ0])],"isStart":true})}),-1.0]])]});}
            var sketch = newSketch(context, id + "F3", { "sketchPlane" : qUnion([Q0])});
            skLineSegment(sketch, "E345", {"start": v(-70.24, -31.76) * mm, "end": v(-70.24, -107.96) * mm});
            skLineSegment(sketch, "E346", {"start": v(-57.54, -31.76) * mm, "end": v(-57.54, -107.96) * mm});
            skArc(sketch, "E347", {"start": v(-57.54, -31.76) * mm, "mid": v(-63.9, -25.41) * mm, "end": v(-70.24, -31.76) * mm});
            skArc(sketch, "E348", {"start": v(-70.24, -107.96) * mm, "mid": v(-63.9, -114.31) * mm, "end": v(-57.54, -107.96) * mm});
            skLineSegment(sketch, "E349", {"start": v(-22.16, 133.36) * mm, "end": v(-22.16, -133.36) * mm});
            skLineSegment(sketch, "E350", {"start": v(-89.3, 0) * mm, "end": v(-22.16, 0) * mm});
            skPoint(sketch, "E350.endSnap0", {"position": v(-22.16, 0) * mm});
            skLineSegment(sketch, "E351", {"start": v(44.98, 0) * mm, "end": v(-22.16, 0) * mm});
            skLineSegment(sketch, "E352.MirrorCS", {"start": v(25.93, -31.76) * mm, "end": v(25.93, -107.96) * mm});
            skLineSegment(sketch, "E353.MirrorCS", {"start": v(13.23, -31.76) * mm, "end": v(13.23, -107.96) * mm});
            skArc(sketch, "E354.MirrorCS", {"start": v(13.23, -31.76) * mm, "mid": v(19.58, -25.41) * mm, "end": v(25.93, -31.76) * mm});
            skArc(sketch, "E355.MirrorCS", {"start": v(25.93, -107.96) * mm, "mid": v(19.58, -114.31) * mm, "end": v(13.23, -107.96) * mm});
            skArc(sketch, "E356.MirrorCS", {"start": v(25.93, 107.96) * mm, "mid": v(19.58, 114.31) * mm, "end": v(13.23, 107.96) * mm});
            skArc(sketch, "E357.MirrorCS", {"start": v(13.23, 31.76) * mm, "mid": v(19.58, 25.41) * mm, "end": v(25.93, 31.76) * mm});
            skLineSegment(sketch, "E358.MirrorCS", {"start": v(13.23, 31.76) * mm, "end": v(13.23, 107.96) * mm});
            skLineSegment(sketch, "E359.MirrorCS", {"start": v(25.93, 31.76) * mm, "end": v(25.93, 107.96) * mm});
            skArc(sketch, "E360.MirrorCS", {"start": v(-57.54, 31.76) * mm, "mid": v(-63.9, 25.41) * mm, "end": v(-70.24, 31.76) * mm});
            skArc(sketch, "E361.MirrorCS", {"start": v(-70.24, 107.96) * mm, "mid": v(-63.9, 114.31) * mm, "end": v(-57.54, 107.96) * mm});
            skLineSegment(sketch, "E362.MirrorCS", {"start": v(-70.24, 31.76) * mm, "end": v(-70.24, 107.96) * mm});
            skLineSegment(sketch, "E363.MirrorCS", {"start": v(-57.54, 31.76) * mm, "end": v(-57.54, 107.96) * mm});
            skSolve(sketch);
        }
        {
            var Q0;
            Q0 = qSketchRegion(id + "F3", true);
            extrude(context, id + "F4", {"entities" : qUnion([Q0]), "operationType" : NewBodyOperationType.REMOVE, "oppositeDirection" : true, "depth" : 30.48 * mm});
        }
        {
            var Q0;
            Q0=makeQuery(id+"F1.opExtrude","SWEPT_FACE",FACE,{"disambiguationData":[OSD([sQuery(id+"F0.wireOp",EDGE,"E301")])]});
            var sketch = newSketch(context, id + "F5", { "sketchPlane" : qUnion([Q0])});
            skLineSegment(sketch, "E364.bottom", {"start": v(-89.3, -133.36) * mm, "end": v(44.98, -133.36) * mm});
            skLineSegment(sketch, "E364.top", {"start": v(-89.3, 133.36) * mm, "end": v(44.98, 133.36) * mm});
            skLineSegment(sketch, "E364.left", {"start": v(-89.3, -133.36) * mm, "end": v(-89.3, 133.36) * mm});
            skLineSegment(sketch, "E364.right", {"start": v(44.98, -133.36) * mm, "end": v(44.98, 133.36) * mm});
            skLineSegment(sketch, "E365", {"start": v(-89.3, 130.19) * mm, "end": v(44.98, 130.19) * mm});
            skLineSegment(sketch, "E366", {"start": v(-89.3, -130.19) * mm, "end": v(44.98, -130.19) * mm});
            skSolve(sketch);
        }
        {
            var Q0;
            {var subQ0=makeQuery(id+"F1.opExtrude","SWEPT_FACE",FACE,{"disambiguationData":[OSD([sQuery(id+"F0.wireOp",EDGE,"E301")])]});Q0=makeQuery(id+"F5.imprint","IMPRINT",FACE,{"disambiguationData":[TD([[makeQuery(id+"F5.imprint","IMPRINT",EDGE,{"derivedFrom":makeQuery(id+"F4.boolean.opBoolean","INTERSECT",EDGE,{"derivedFrom":[subQ0,makeQuery(id+"F4.opExtrude","SWEPT_FACE",FACE,{"disambiguationData":[OSD([sQuery(id+"F3.wireOp",EDGE,"E345")])]})]})}),1.0]])]});}
            var Q1;
            {var subQ0=makeQuery(id+"F1.opExtrude","SWEPT_FACE",FACE,{"disambiguationData":[OSD([sQuery(id+"F0.wireOp",EDGE,"E301")])]});Q1=makeQuery(id+"F5.imprint","IMPRINT",FACE,{"disambiguationData":[TD([[makeQuery(id+"F5.imprint","IMPRINT",EDGE,{"derivedFrom":makeQuery(id+"F4.boolean.opBoolean","INTERSECT",EDGE,{"derivedFrom":[subQ0,makeQuery(id+"F4.opExtrude","SWEPT_FACE",FACE,{"disambiguationData":[OSD([sQuery(id+"F3.wireOp",EDGE,"E352.MirrorCS")])]})]})}),-1.0]])]});}
            var Q2;
            {var subQ0=makeQuery(id+"F1.opExtrude","SWEPT_FACE",FACE,{"disambiguationData":[OSD([sQuery(id+"F0.wireOp",EDGE,"E301")])]});Q2=makeQuery(id+"F5.imprint","IMPRINT",FACE,{"disambiguationData":[TD([[makeQuery(id+"F5.imprint","IMPRINT",EDGE,{"derivedFrom":makeQuery(id+"F4.boolean.opBoolean","INTERSECT",EDGE,{"derivedFrom":[subQ0,makeQuery(id+"F4.opExtrude","SWEPT_FACE",FACE,{"disambiguationData":[OSD([sQuery(id+"F3.wireOp",EDGE,"E356.MirrorCS")])]})]})}),1.0]])]});}
            var Q3;
            {var subQ0=makeQuery(id+"F1.opExtrude","SWEPT_FACE",FACE,{"disambiguationData":[OSD([sQuery(id+"F0.wireOp",EDGE,"E301")])]});Q3=makeQuery(id+"F5.imprint","IMPRINT",FACE,{"disambiguationData":[TD([[makeQuery(id+"F5.imprint","IMPRINT",EDGE,{"derivedFrom":makeQuery(id+"F4.boolean.opBoolean","INTERSECT",EDGE,{"derivedFrom":[subQ0,makeQuery(id+"F4.opExtrude","SWEPT_FACE",FACE,{"disambiguationData":[OSD([sQuery(id+"F3.wireOp",EDGE,"E360.MirrorCS")])]})]})}),-1.0]])]});}
            var Q4;
            {var subQ1=sQuery(id+"F5.wireOp",EDGE,"E365");Q4=makeQuery(id+"F5.imprint","IMPRINT",FACE,{"disambiguationData":[TD([[makeQuery(id+"F5.imprint","IMPRINT",EDGE,{"derivedFrom":subQ1}),-1.0]])]});}
            extrude(context, id + "F6", {"entities" : qUnion([Q0, Q1, Q2, Q3, Q4]), "operationType" : NewBodyOperationType.REMOVE, "oppositeDirection" : true, "depth" : 26.67 * mm});
        }
        {
            var Q0;
            Q0=makeQuery(id+"F1.opExtrude","SWEPT_FACE",FACE,{"disambiguationData":[OSD([sQuery(id+"F0.wireOp",EDGE,"E305"),sQuery(id+"F0.wireOp",EDGE,"E318")])]});
            var sketch = newSketch(context, id + "F7", { "sketchPlane" : qUnion([Q0])});
            skLineSegment(sketch, "E367", {"start": v(-117.4, -133.36) * mm, "end": v(-105.08, -133.36) * mm});
            skLineSegment(sketch, "E368", {"start": v(-105.08, -133.36) * mm, "end": v(-105.08, -121.03) * mm});
            skArc(sketch, "E369", {"start": v(-105.08, -133.36) * mm, "mid": v(-113.8, -129.75) * mm, "end": v(-117.4, -121.03) * mm});
            skLineSegment(sketch, "E370", {"start": v(-117.4, -133.36) * mm, "end": v(73.1, -133.36) * mm});
            skLineSegment(sketch, "E371", {"start": v(-22.16, -133.36) * mm, "end": v(-22.16, 133.36) * mm});
            skLineSegment(sketch, "E372", {"start": v(-22.16, 0) * mm, "end": v(-117.4, 0) * mm});
            skArc(sketch, "E373.MirrorCS", {"start": v(60.76, -133.36) * mm, "mid": v(69.48, -129.75) * mm, "end": v(73.1, -121.03) * mm});
            skLineSegment(sketch, "E374", {"start": v(-117.4, -121.03) * mm, "end": v(-117.4, -133.36) * mm});
            skLineSegment(sketch, "E375", {"start": v(73.1, -121.03) * mm, "end": v(73.1, -133.36) * mm});
            skLineSegment(sketch, "E376.MirrorCS", {"start": v(-117.4, 133.36) * mm, "end": v(-105.08, 133.36) * mm});
            skLineSegment(sketch, "E377.MirrorCS", {"start": v(-117.4, 121.03) * mm, "end": v(-117.4, 133.36) * mm});
            skLineSegment(sketch, "E378.MirrorCS", {"start": v(73.1, 121.03) * mm, "end": v(73.1, 133.36) * mm});
            skLineSegment(sketch, "E379.MirrorCS", {"start": v(-105.08, 133.36) * mm, "end": v(-105.08, 121.03) * mm});
            skArc(sketch, "E380.MirrorCS", {"start": v(-105.08, 133.36) * mm, "mid": v(-113.8, 129.75) * mm, "end": v(-117.4, 121.03) * mm});
            skArc(sketch, "E381.MirrorCS", {"start": v(60.76, 133.36) * mm, "mid": v(69.48, 129.75) * mm, "end": v(73.1, 121.03) * mm});
            skLineSegment(sketch, "E382.MirrorCS", {"start": v(-117.4, 133.36) * mm, "end": v(73.1, 133.36) * mm});
            skCircle(sketch, "E383", {"center": v(-107.88, -95.26) * mm, "radius": 3.34 * mm});
            skCircle(sketch, "E384.MirrorC", {"center": v(63.57, -95.26) * mm, "radius": 3.34 * mm});
            skCircle(sketch, "E385.MirrorC", {"center": v(-107.88, 95.26) * mm, "radius": 3.34 * mm});
            skCircle(sketch, "E386.MirrorC", {"center": v(63.57, 95.26) * mm, "radius": 3.34 * mm});
            skSolve(sketch);
        }
        {
            var Q0;
            {var subQ0=sQuery(id+"F7.wireOp",EDGE,"E377.MirrorCS");Q0=makeQuery(id+"F7.imprint","IMPRINT",FACE,{"disambiguationData":[TD([[makeQuery(id+"F7.imprint","IMPRINT",EDGE,{"derivedFrom":subQ0}),-1.0]])]});}
            var Q1;
            {var subQ0=sQuery(id+"F7.wireOp",EDGE,"E378.MirrorCS");Q1=makeQuery(id+"F7.imprint","IMPRINT",FACE,{"disambiguationData":[TD([[makeQuery(id+"F7.imprint","IMPRINT",EDGE,{"derivedFrom":subQ0}),1.0]])]});}
            var Q2;
            {var subQ2=sQuery(id+"F7.wireOp",EDGE,"E373.MirrorCS");Q2=makeQuery(id+"F7.imprint","IMPRINT",FACE,{"disambiguationData":[TD([[makeQuery(id+"F7.imprint","IMPRINT",EDGE,{"derivedFrom":subQ2}),-1.0]])]});}
            var Q3;
            {var subQ0=sQuery(id+"F7.wireOp",EDGE,"E369");Q3=makeQuery(id+"F7.imprint","IMPRINT",FACE,{"disambiguationData":[TD([[makeQuery(id+"F7.imprint","IMPRINT",EDGE,{"derivedFrom":subQ0}),1.0]])]});}
            var Q4;
            Q4=makeQuery(id+"F7.imprint","IMPRINT",FACE,{"disambiguationData":[TD([[makeQuery(id+"F7.imprint","IMPRINT",EDGE,{"derivedFrom":sQuery(id+"F7.wireOp",EDGE,"E383")}),1.0]])]});
            var Q5;
            Q5=makeQuery(id+"F7.imprint","IMPRINT",FACE,{"disambiguationData":[TD([[makeQuery(id+"F7.imprint","IMPRINT",EDGE,{"derivedFrom":sQuery(id+"F7.wireOp",EDGE,"E384.MirrorC")}),-1.0]])]});
            var Q6;
            Q6=makeQuery(id+"F7.imprint","IMPRINT",FACE,{"disambiguationData":[TD([[makeQuery(id+"F7.imprint","IMPRINT",EDGE,{"derivedFrom":sQuery(id+"F7.wireOp",EDGE,"E386.MirrorC")}),1.0]])]});
            var Q7;
            Q7=makeQuery(id+"F7.imprint","IMPRINT",FACE,{"disambiguationData":[TD([[makeQuery(id+"F7.imprint","IMPRINT",EDGE,{"derivedFrom":sQuery(id+"F7.wireOp",EDGE,"E385.MirrorC")}),-1.0]])]});
            extrude(context, id + "F8", {"entities" : qUnion([Q0, Q1, Q2, Q3, Q4, Q5, Q6, Q7]), "operationType" : NewBodyOperationType.REMOVE, "oppositeDirection" : true, "depth" : 25.4 * mm});
        }
        {
            var Q0;
            Q0=makeQuery(id+"F6.boolean.opBoolean","COPY",FACE,{"derivedFrom":makeQuery(id+"F6.opExtrude","CAP_FACE",FACE,{"disambiguationData":[OSD([sQuery(id+"F5.wireOp",EDGE,"E364.left"),sQuery(id+"F5.wireOp",EDGE,"E364.right"),sQuery(id+"F5.wireOp",EDGE,"E365"),sQuery(id+"F5.wireOp",EDGE,"E366")])],"isStart":false})});
            var sketch = newSketch(context, id + "F9", { "sketchPlane" : qUnion([Q0])});
            skLineSegment(sketch, "E387", {"start": v(231.5, -77.5) * mm, "end": v(231.5, -147.22) * mm});
            skLineSegment(sketch, "E388", {"start": v(172.89, -77.5) * mm, "end": v(231.5, -77.5) * mm});
            skLineSegment(sketch, "E389", {"start": v(202.19, -77.5) * mm, "end": v(202.19, -64.8) * mm});
            skLineSegment(sketch, "E390", {"start": v(202.19, -71.16) * mm, "end": v(164.63, -71.16) * mm});
            skLineSegment(sketch, "E391", {"start": v(186.88, -64.8) * mm, "end": v(186.88, -160.03) * mm});
            skCircle(sketch, "E392", {"center": v(172.89, -77.5) * mm, "radius": 4.76 * mm});
            skLineSegment(sketch, "E393", {"start": v(202.19, -64.8) * mm, "end": v(164.63, -64.8) * mm});
            skLineSegment(sketch, "E394", {"start": v(164.63, -64.8) * mm, "end": v(164.63, -160.03) * mm});
            skLineSegment(sketch, "E395", {"start": v(164.63, -160.03) * mm, "end": v(202.19, -160.03) * mm});
            skLineSegment(sketch, "E396.MirrorCS", {"start": v(202.19, -64.8) * mm, "end": v(239.74, -64.8) * mm});
            skLineSegment(sketch, "E397.MirrorCS", {"start": v(239.74, -64.8) * mm, "end": v(239.74, -160.03) * mm});
            skLineSegment(sketch, "E398.MirrorCS", {"start": v(239.74, -160.03) * mm, "end": v(202.19, -160.03) * mm});
            skCircle(sketch, "E399.MirrorC", {"center": v(231.5, -77.5) * mm, "radius": 4.76 * mm});
            skLineSegment(sketch, "E400", {"start": v(164.63, -112.41) * mm, "end": v(239.74, -112.41) * mm});
            skCircle(sketch, "E401.MirrorC", {"center": v(172.89, -147.32) * mm, "radius": 4.76 * mm});
            skCircle(sketch, "E402.MirrorC", {"center": v(231.5, -147.32) * mm, "radius": 4.76 * mm});
            skSolve(sketch);
        }
        {
            var Q0;
            Q0 = qSketchRegion(id + "F9", true);
            var Q1;
            {var subQ6=sQuery(id+"F9.wireOp",EDGE,"E400");var subQ8=sQuery(id+"F9.wireOp",EDGE,"E387");var subQ9=makeQuery(id+"F9.imprint","INTERSECT",VERTEX,{"derivedFrom":[subQ8,subQ6]});Q1=makeQuery(id+"F9.imprint","IMPRINT",FACE,{"disambiguationData":[TD([[makeQuery(id+"F9.imprint","IMPRINT",EDGE,{"disambiguationData":[TD([[subQ9,1.0]])],"derivedFrom":subQ8}),-1.0]])]});}
            var Q2;
            {var subQ0=sQuery(id+"F9.wireOp",EDGE,"E389");var subQ1=sQuery(id+"F9.wireOp",EDGE,"E388");var subQ2=makeQuery(id+"F9.imprint","INTERSECT",VERTEX,{"derivedFrom":[subQ1,subQ0]});Q2=makeQuery(id+"F9.imprint","IMPRINT",FACE,{"disambiguationData":[TD([[makeQuery(id+"F9.imprint","IMPRINT",EDGE,{"disambiguationData":[TD([[subQ2,1.0]])],"derivedFrom":subQ1}),1.0]])]});}
            extrude(context, id + "F10", {"entities" : qUnion([Q0, Q1, Q2]), "depth" : 12.7 * mm});
        }
    });
